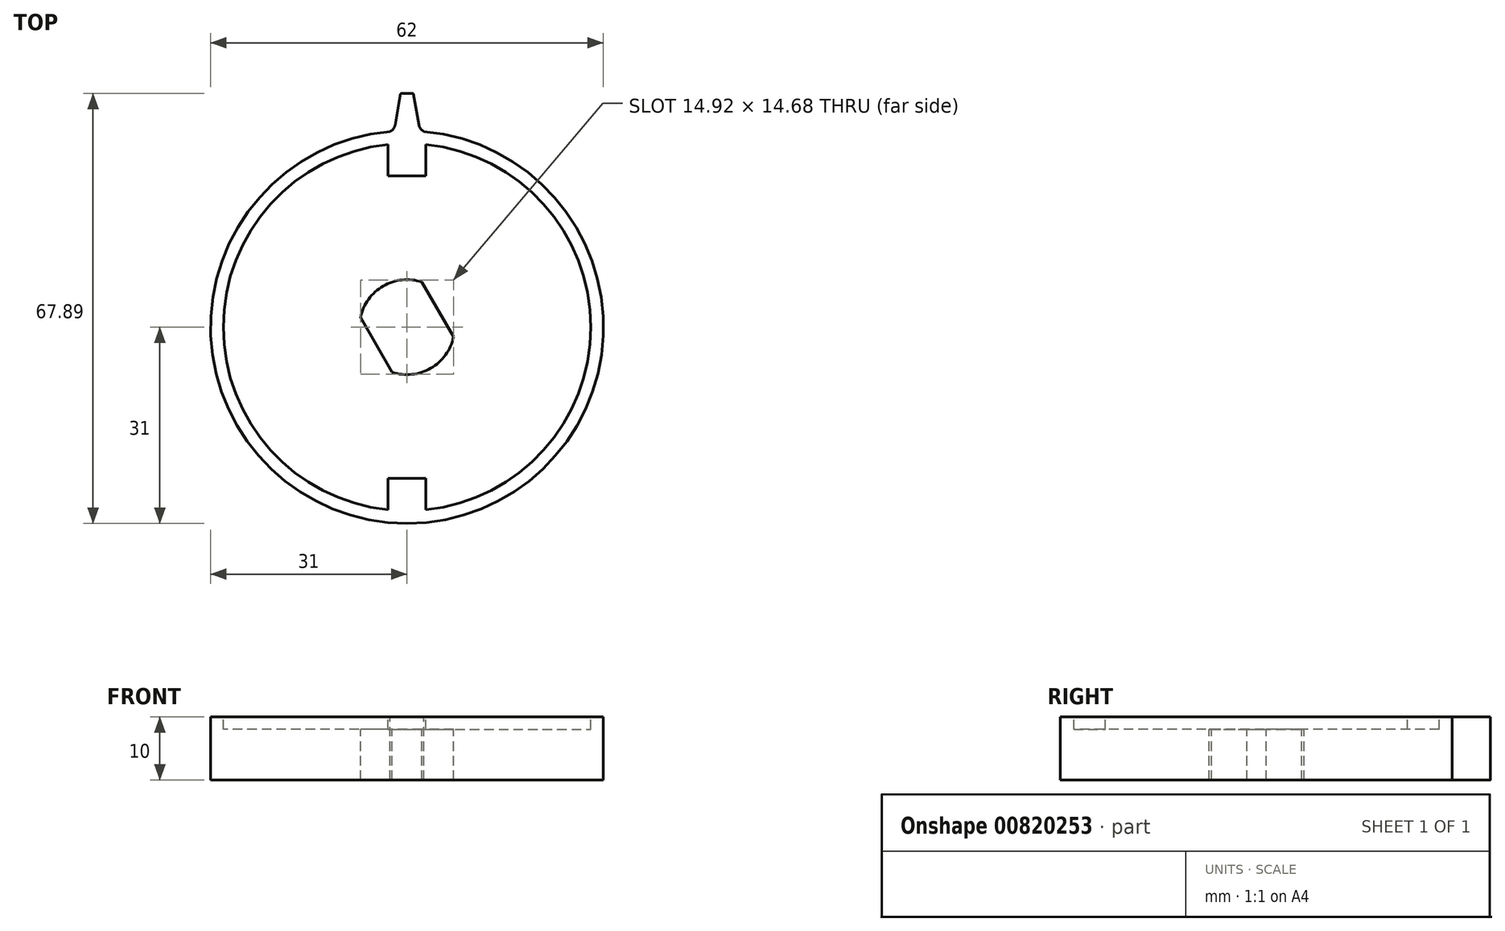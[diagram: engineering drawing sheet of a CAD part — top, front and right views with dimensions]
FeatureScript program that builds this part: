
annotation { "Feature Type Name" : "Feature", "Feature Type Description" : "" }
export const myFeature = defineFeature(function(context is Context, id is Id, definition is map)
    precondition{}
    {
        {
            var Q0;
            Q0=qCreatedBy(makeId("Top.planeOp"),FACE);
            var sketch = newSketch(context, id + "F0", { "sketchPlane" : qUnion([Q0])});
            skCircle(sketch, "E0", {"center": v(0, 0) * mm, "radius": 31 * mm});
            skSolve(sketch);
        }
        {
            var Q0;
            Q0 = qSketchRegion(id + "F0", true);
            extrude(context, id + "F1", {"entities" : qUnion([Q0]), "depth" : 10 * mm, "offsetDistance" : 25 * mm});
        }
        {
            var Q0;
            Q0=makeQuery(id+"F1.opExtrude","CAP_FACE",FACE,{"disambiguationData":[OSD([sQuery(id+"F0.wireOp",EDGE,"E0")])],"isStart":false});
            var sketch = newSketch(context, id + "F2", { "sketchPlane" : qUnion([Q0])});
            skLineSegment(sketch, "E1", {"start": v(-0.92, 36.89) * mm, "end": v(0.92, 36.89) * mm});
            skLineSegment(sketch, "E2", {"start": v(-1.01, 36.8) * mm, "end": v(-1.87, 31.96) * mm});
            skArc(sketch, "E3", {"start": v(-1.87, 31.96) * mm, "mid": v(-2.14, 31.33) * mm, "end": v(-2.66, 30.89) * mm});
            skLineSegment(sketch, "E4.MirrorCS", {"start": v(1.01, 36.8) * mm, "end": v(1.87, 31.96) * mm});
            skArc(sketch, "E5.MirrorCS", {"start": v(1.87, 31.96) * mm, "mid": v(2.14, 31.33) * mm, "end": v(2.66, 30.89) * mm});
            skArc(sketch, "E6.0", {"start": v(2.66, 30.89) * mm, "mid": v(0, 31) * mm, "end": v(-2.66, 30.89) * mm});
            skPoint(sketch, "E7.visualSharp", {"position": v(-1, 36.89) * mm});
            skArc(sketch, "E7.filletArc", {"start": v(-0.92, 36.89) * mm, "mid": v(-0.98, 36.86) * mm, "end": v(-1.01, 36.8) * mm});
            skPoint(sketch, "E8.visualSharp", {"position": v(1, 36.89) * mm});
            skArc(sketch, "E8.filletArc", {"start": v(1.01, 36.8) * mm, "mid": v(0.98, 36.86) * mm, "end": v(0.92, 36.89) * mm});
            skSolve(sketch);
        }
        {
            var Q0;
            Q0=makeQuery(id+"F2.imprint","IMPRINT",FACE,{"disambiguationData":[TD([[makeQuery(id+"F2.imprint","IMPRINT",EDGE,{"derivedFrom":sQuery(id+"F2.wireOp",EDGE,"E1")}),-1.0]])]});
            extrude(context, id + "F3", {"entities" : qUnion([Q0]), "operationType" : NewBodyOperationType.ADD, "oppositeDirection" : true, "depth" : 10 * mm, "offsetDistance" : 25 * mm});
        }
        {
            var Q0;
            {var subQ0=sQuery(id+"F2.wireOp",EDGE,"E8.filletArc");var subQ1=sQuery(id+"F2.wireOp",EDGE,"E7.filletArc");var subQ2=sQuery(id+"F2.wireOp",EDGE,"E6.0");var subQ3=sQuery(id+"F2.wireOp",EDGE,"E5.MirrorCS");var subQ4=sQuery(id+"F2.wireOp",EDGE,"E4.MirrorCS");var subQ5=sQuery(id+"F2.wireOp",EDGE,"E3");var subQ6=sQuery(id+"F2.wireOp",EDGE,"E2");var subQ7=sQuery(id+"F2.wireOp",EDGE,"E1");Q0=makeQuery(id+"FxFIOQCDVqTxC9O_1.33.F3.boolean.opBoolean","MERGE",FACE,{"derivedFrom":[makeQuery(id+"FxFIOQCDVqTxC9O_1.32.F3.boolean.opBoolean","MERGE",FACE,{"derivedFrom":[makeQuery(id+"FxFIOQCDVqTxC9O_1.31.F3.boolean.opBoolean","MERGE",FACE,{"derivedFrom":[makeQuery(id+"FxFIOQCDVqTxC9O_1.30.F3.boolean.opBoolean","MERGE",FACE,{"derivedFrom":[makeQuery(id+"FxFIOQCDVqTxC9O_1.29.F3.boolean.opBoolean","MERGE",FACE,{"derivedFrom":[makeQuery(id+"FxFIOQCDVqTxC9O_1.28.F3.boolean.opBoolean","MERGE",FACE,{"derivedFrom":[makeQuery(id+"FxFIOQCDVqTxC9O_1.27.F3.boolean.opBoolean","MERGE",FACE,{"derivedFrom":[makeQuery(id+"FxFIOQCDVqTxC9O_1.26.F3.boolean.opBoolean","MERGE",FACE,{"derivedFrom":[makeQuery(id+"FxFIOQCDVqTxC9O_1.25.F3.boolean.opBoolean","MERGE",FACE,{"derivedFrom":[makeQuery(id+"FxFIOQCDVqTxC9O_1.24.F3.boolean.opBoolean","MERGE",FACE,{"derivedFrom":[makeQuery(id+"FxFIOQCDVqTxC9O_1.23.F3.boolean.opBoolean","MERGE",FACE,{"derivedFrom":[makeQuery(id+"FxFIOQCDVqTxC9O_1.22.F3.boolean.opBoolean","MERGE",FACE,{"derivedFrom":[makeQuery(id+"FxFIOQCDVqTxC9O_1.21.F3.boolean.opBoolean","MERGE",FACE,{"derivedFrom":[makeQuery(id+"FxFIOQCDVqTxC9O_1.20.F3.boolean.opBoolean","MERGE",FACE,{"derivedFrom":[makeQuery(id+"FxFIOQCDVqTxC9O_1.19.F3.boolean.opBoolean","MERGE",FACE,{"derivedFrom":[makeQuery(id+"FxFIOQCDVqTxC9O_1.18.F3.boolean.opBoolean","MERGE",FACE,{"derivedFrom":[makeQuery(id+"FxFIOQCDVqTxC9O_1.17.F3.boolean.opBoolean","MERGE",FACE,{"derivedFrom":[makeQuery(id+"FxFIOQCDVqTxC9O_1.16.F3.boolean.opBoolean","MERGE",FACE,{"derivedFrom":[makeQuery(id+"FxFIOQCDVqTxC9O_1.15.F3.boolean.opBoolean","MERGE",FACE,{"derivedFrom":[makeQuery(id+"FxFIOQCDVqTxC9O_1.14.F3.boolean.opBoolean","MERGE",FACE,{"derivedFrom":[makeQuery(id+"FxFIOQCDVqTxC9O_1.13.F3.boolean.opBoolean","MERGE",FACE,{"derivedFrom":[makeQuery(id+"FxFIOQCDVqTxC9O_1.12.F3.boolean.opBoolean","MERGE",FACE,{"derivedFrom":[makeQuery(id+"FxFIOQCDVqTxC9O_1.11.F3.boolean.opBoolean","MERGE",FACE,{"derivedFrom":[makeQuery(id+"FxFIOQCDVqTxC9O_1.10.F3.boolean.opBoolean","MERGE",FACE,{"derivedFrom":[makeQuery(id+"FxFIOQCDVqTxC9O_1.9.F3.boolean.opBoolean","MERGE",FACE,{"derivedFrom":[makeQuery(id+"FxFIOQCDVqTxC9O_1.8.F3.boolean.opBoolean","MERGE",FACE,{"derivedFrom":[makeQuery(id+"FxFIOQCDVqTxC9O_1.7.F3.boolean.opBoolean","MERGE",FACE,{"derivedFrom":[makeQuery(id+"FxFIOQCDVqTxC9O_1.6.F3.boolean.opBoolean","MERGE",FACE,{"derivedFrom":[makeQuery(id+"FxFIOQCDVqTxC9O_1.5.F3.boolean.opBoolean","MERGE",FACE,{"derivedFrom":[makeQuery(id+"FxFIOQCDVqTxC9O_1.4.F3.boolean.opBoolean","MERGE",FACE,{"derivedFrom":[makeQuery(id+"FxFIOQCDVqTxC9O_1.3.F3.boolean.opBoolean","MERGE",FACE,{"derivedFrom":[makeQuery(id+"FxFIOQCDVqTxC9O_1.2.F3.boolean.opBoolean","MERGE",FACE,{"derivedFrom":[makeQuery(id+"FxFIOQCDVqTxC9O_1.1.F3.boolean.opBoolean","MERGE",FACE,{"derivedFrom":[makeQuery(id+"F3.boolean.opBoolean","MERGE",FACE,{"derivedFrom":[makeQuery(id+"F1.opExtrude","CAP_FACE",FACE,{"disambiguationData":[OSD([sQuery(id+"F0.wireOp",EDGE,"E0")])],"isStart":false}),makeQuery(id+"F3.opExtrude","CAP_FACE",FACE,{"disambiguationData":[OSD([subQ7,subQ6,subQ5,subQ4,subQ3,subQ2,subQ1,subQ0])],"isStart":true})]}),makeQuery(id+"FxFIOQCDVqTxC9O_1.1.F3.opExtrude","CAP_FACE",FACE,{"disambiguationData":[OSD([subQ7,subQ6,subQ5,subQ4,subQ3,subQ2,subQ1,subQ0])],"isStart":true})]}),makeQuery(id+"FxFIOQCDVqTxC9O_1.2.F3.opExtrude","CAP_FACE",FACE,{"disambiguationData":[OSD([subQ7,subQ6,subQ5,subQ4,subQ3,subQ2,subQ1,subQ0])],"isStart":true})]}),makeQuery(id+"FxFIOQCDVqTxC9O_1.3.F3.opExtrude","CAP_FACE",FACE,{"disambiguationData":[OSD([subQ7,subQ6,subQ5,subQ4,subQ3,subQ2,subQ1,subQ0])],"isStart":true})]}),makeQuery(id+"FxFIOQCDVqTxC9O_1.4.F3.opExtrude","CAP_FACE",FACE,{"disambiguationData":[OSD([subQ7,subQ6,subQ5,subQ4,subQ3,subQ2,subQ1,subQ0])],"isStart":true})]}),makeQuery(id+"FxFIOQCDVqTxC9O_1.5.F3.opExtrude","CAP_FACE",FACE,{"disambiguationData":[OSD([subQ7,subQ6,subQ5,subQ4,subQ3,subQ2,subQ1,subQ0])],"isStart":true})]}),makeQuery(id+"FxFIOQCDVqTxC9O_1.6.F3.opExtrude","CAP_FACE",FACE,{"disambiguationData":[OSD([subQ7,subQ6,subQ5,subQ4,subQ3,subQ2,subQ1,subQ0])],"isStart":true})]}),makeQuery(id+"FxFIOQCDVqTxC9O_1.7.F3.opExtrude","CAP_FACE",FACE,{"disambiguationData":[OSD([subQ7,subQ6,subQ5,subQ4,subQ3,subQ2,subQ1,subQ0])],"isStart":true})]}),makeQuery(id+"FxFIOQCDVqTxC9O_1.8.F3.opExtrude","CAP_FACE",FACE,{"disambiguationData":[OSD([subQ7,subQ6,subQ5,subQ4,subQ3,subQ2,subQ1,subQ0])],"isStart":true})]}),makeQuery(id+"FxFIOQCDVqTxC9O_1.9.F3.opExtrude","CAP_FACE",FACE,{"disambiguationData":[OSD([subQ7,subQ6,subQ5,subQ4,subQ3,subQ2,subQ1,subQ0])],"isStart":true})]}),makeQuery(id+"FxFIOQCDVqTxC9O_1.10.F3.opExtrude","CAP_FACE",FACE,{"disambiguationData":[OSD([subQ7,subQ6,subQ5,subQ4,subQ3,subQ2,subQ1,subQ0])],"isStart":true})]}),makeQuery(id+"FxFIOQCDVqTxC9O_1.11.F3.opExtrude","CAP_FACE",FACE,{"disambiguationData":[OSD([subQ7,subQ6,subQ5,subQ4,subQ3,subQ2,subQ1,subQ0])],"isStart":true})]}),makeQuery(id+"FxFIOQCDVqTxC9O_1.12.F3.opExtrude","CAP_FACE",FACE,{"disambiguationData":[OSD([subQ7,subQ6,subQ5,subQ4,subQ3,subQ2,subQ1,subQ0])],"isStart":true})]}),makeQuery(id+"FxFIOQCDVqTxC9O_1.13.F3.opExtrude","CAP_FACE",FACE,{"disambiguationData":[OSD([subQ7,subQ6,subQ5,subQ4,subQ3,subQ2,subQ1,subQ0])],"isStart":true})]}),makeQuery(id+"FxFIOQCDVqTxC9O_1.14.F3.opExtrude","CAP_FACE",FACE,{"disambiguationData":[OSD([subQ7,subQ6,subQ5,subQ4,subQ3,subQ2,subQ1,subQ0])],"isStart":true})]}),makeQuery(id+"FxFIOQCDVqTxC9O_1.15.F3.opExtrude","CAP_FACE",FACE,{"disambiguationData":[OSD([subQ7,subQ6,subQ5,subQ4,subQ3,subQ2,subQ1,subQ0])],"isStart":true})]}),makeQuery(id+"FxFIOQCDVqTxC9O_1.16.F3.opExtrude","CAP_FACE",FACE,{"disambiguationData":[OSD([subQ7,subQ6,subQ5,subQ4,subQ3,subQ2,subQ1,subQ0])],"isStart":true})]}),makeQuery(id+"FxFIOQCDVqTxC9O_1.17.F3.opExtrude","CAP_FACE",FACE,{"disambiguationData":[OSD([subQ7,subQ6,subQ5,subQ4,subQ3,subQ2,subQ1,subQ0])],"isStart":true})]}),makeQuery(id+"FxFIOQCDVqTxC9O_1.18.F3.opExtrude","CAP_FACE",FACE,{"disambiguationData":[OSD([subQ7,subQ6,subQ5,subQ4,subQ3,subQ2,subQ1,subQ0])],"isStart":true})]}),makeQuery(id+"FxFIOQCDVqTxC9O_1.19.F3.opExtrude","CAP_FACE",FACE,{"disambiguationData":[OSD([subQ7,subQ6,subQ5,subQ4,subQ3,subQ2,subQ1,subQ0])],"isStart":true})]}),makeQuery(id+"FxFIOQCDVqTxC9O_1.20.F3.opExtrude","CAP_FACE",FACE,{"disambiguationData":[OSD([subQ7,subQ6,subQ5,subQ4,subQ3,subQ2,subQ1,subQ0])],"isStart":true})]}),makeQuery(id+"FxFIOQCDVqTxC9O_1.21.F3.opExtrude","CAP_FACE",FACE,{"disambiguationData":[OSD([subQ7,subQ6,subQ5,subQ4,subQ3,subQ2,subQ1,subQ0])],"isStart":true})]}),makeQuery(id+"FxFIOQCDVqTxC9O_1.22.F3.opExtrude","CAP_FACE",FACE,{"disambiguationData":[OSD([subQ7,subQ6,subQ5,subQ4,subQ3,subQ2,subQ1,subQ0])],"isStart":true})]}),makeQuery(id+"FxFIOQCDVqTxC9O_1.23.F3.opExtrude","CAP_FACE",FACE,{"disambiguationData":[OSD([subQ7,subQ6,subQ5,subQ4,subQ3,subQ2,subQ1,subQ0])],"isStart":true})]}),makeQuery(id+"FxFIOQCDVqTxC9O_1.24.F3.opExtrude","CAP_FACE",FACE,{"disambiguationData":[OSD([subQ7,subQ6,subQ5,subQ4,subQ3,subQ2,subQ1,subQ0])],"isStart":true})]}),makeQuery(id+"FxFIOQCDVqTxC9O_1.25.F3.opExtrude","CAP_FACE",FACE,{"disambiguationData":[OSD([subQ7,subQ6,subQ5,subQ4,subQ3,subQ2,subQ1,subQ0])],"isStart":true})]}),makeQuery(id+"FxFIOQCDVqTxC9O_1.26.F3.opExtrude","CAP_FACE",FACE,{"disambiguationData":[OSD([subQ7,subQ6,subQ5,subQ4,subQ3,subQ2,subQ1,subQ0])],"isStart":true})]}),makeQuery(id+"FxFIOQCDVqTxC9O_1.27.F3.opExtrude","CAP_FACE",FACE,{"disambiguationData":[OSD([subQ7,subQ6,subQ5,subQ4,subQ3,subQ2,subQ1,subQ0])],"isStart":true})]}),makeQuery(id+"FxFIOQCDVqTxC9O_1.28.F3.opExtrude","CAP_FACE",FACE,{"disambiguationData":[OSD([subQ7,subQ6,subQ5,subQ4,subQ3,subQ2,subQ1,subQ0])],"isStart":true})]}),makeQuery(id+"FxFIOQCDVqTxC9O_1.29.F3.opExtrude","CAP_FACE",FACE,{"disambiguationData":[OSD([subQ7,subQ6,subQ5,subQ4,subQ3,subQ2,subQ1,subQ0])],"isStart":true})]}),makeQuery(id+"FxFIOQCDVqTxC9O_1.30.F3.opExtrude","CAP_FACE",FACE,{"disambiguationData":[OSD([subQ7,subQ6,subQ5,subQ4,subQ3,subQ2,subQ1,subQ0])],"isStart":true})]}),makeQuery(id+"FxFIOQCDVqTxC9O_1.31.F3.opExtrude","CAP_FACE",FACE,{"disambiguationData":[OSD([subQ7,subQ6,subQ5,subQ4,subQ3,subQ2,subQ1,subQ0])],"isStart":true})]}),makeQuery(id+"FxFIOQCDVqTxC9O_1.32.F3.opExtrude","CAP_FACE",FACE,{"disambiguationData":[OSD([subQ7,subQ6,subQ5,subQ4,subQ3,subQ2,subQ1,subQ0])],"isStart":true})]}),makeQuery(id+"FxFIOQCDVqTxC9O_1.33.F3.opExtrude","CAP_FACE",FACE,{"disambiguationData":[OSD([subQ7,subQ6,subQ5,subQ4,subQ3,subQ2,subQ1,subQ0])],"isStart":true})]});}
            var sketch = newSketch(context, id + "F4", { "sketchPlane" : qUnion([Q0])});
            skArc(sketch, "E9.0", {"start": v(-3, 30.85) * mm, "mid": v(-31, 0) * mm, "end": v(-3, -30.85) * mm, "construction": true});
            skLineSegment(sketch, "E10", {"start": v(-3, 30.85) * mm, "end": v(-3, 23.85) * mm});
            skLineSegment(sketch, "E11", {"start": v(-3, 23.85) * mm, "end": v(3, 23.85) * mm});
            skLineSegment(sketch, "E12", {"start": v(3, 23.85) * mm, "end": v(3, 30.85) * mm});
            skLineSegment(sketch, "E13", {"start": v(-53.63, 0) * mm, "end": v(44.5, 0) * mm, "construction": true});
            skLineSegment(sketch, "E14.MirrorCS", {"start": v(-3, -30.85) * mm, "end": v(-3, -23.85) * mm});
            skLineSegment(sketch, "E15.MirrorCS", {"start": v(-3, -23.85) * mm, "end": v(3, -23.85) * mm});
            skLineSegment(sketch, "E16.MirrorCS", {"start": v(3, -23.85) * mm, "end": v(3, -30.85) * mm});
            skArc(sketch, "E17.trimOffspring", {"start": v(3, -30.85) * mm, "mid": v(31, 0) * mm, "end": v(3, 30.85) * mm, "construction": true});
            skCircle(sketch, "E18", {"center": v(0, 0) * mm, "radius": 29 * mm});
            skSolve(sketch);
        }
        {
            var Q0;
            {var subQ1=sQuery(id+"F4.wireOp",EDGE,"E11");Q0=makeQuery(id+"F4.imprint","IMPRINT",FACE,{"disambiguationData":[TD([[makeQuery(id+"F4.imprint","IMPRINT",EDGE,{"derivedFrom":subQ1}),-1.0]])]});}
            extrude(context, id + "F5", {"entities" : qUnion([Q0]), "operationType" : NewBodyOperationType.REMOVE, "oppositeDirection" : true, "depth" : 2 * mm, "offsetDistance" : 25 * mm});
        }
        {
            var Q0;
            Q0=makeQuery(id+"F5.boolean.opBoolean","COPY",FACE,{"derivedFrom":makeQuery(id+"F5.opExtrude","CAP_FACE",FACE,{"disambiguationData":[OSD([sQuery(id+"F4.wireOp",EDGE,"E10"),sQuery(id+"F4.wireOp",EDGE,"E11"),sQuery(id+"F4.wireOp",EDGE,"E12"),sQuery(id+"F4.wireOp",EDGE,"E14.MirrorCS"),sQuery(id+"F4.wireOp",EDGE,"E15.MirrorCS"),sQuery(id+"F4.wireOp",EDGE,"E16.MirrorCS"),sQuery(id+"F4.wireOp",EDGE,"E18")])],"isStart":false})});
            var sketch = newSketch(context, id + "F6", { "sketchPlane" : qUnion([Q0])});
            skLineSegment(sketch, "E19", {"start": v(8.88, -15.38) * mm, "end": v(-6.48, 11.22) * mm, "construction": true});
            skLineSegment(sketch, "E20", {"start": v(-2.34, -7.13) * mm, "end": v(-7.34, 1.54) * mm});
            skLineSegment(sketch, "E21", {"start": v(7.34, -1.54) * mm, "end": v(2.34, 7.13) * mm});
            skLineSegment(sketch, "E22", {"start": v(-2.34, -7.13) * mm, "end": v(7.34, -1.54) * mm, "construction": true});
            skArc(sketch, "E23", {"start": v(-2.34, -7.13) * mm, "mid": v(3.75, -6.5) * mm, "end": v(7.34, -1.54) * mm});
            skArc(sketch, "E24.trimOffspring", {"start": v(2.34, 7.13) * mm, "mid": v(-3.75, 6.5) * mm, "end": v(-7.34, 1.54) * mm});
            skSolve(sketch);
        }
        {
            var Q0;
            Q0=makeQuery(id+"F6.imprint","IMPRINT",FACE,{"disambiguationData":[TD([[makeQuery(id+"F6.imprint","IMPRINT",EDGE,{"derivedFrom":sQuery(id+"F6.wireOp",EDGE,"E20")}),-1.0]])]});
            extrude(context, id + "F7", {"entities" : qUnion([Q0]), "operationType" : NewBodyOperationType.REMOVE, "oppositeDirection" : true, "depth" : 25 * mm, "offsetDistance" : 25 * mm});
        }
    });
